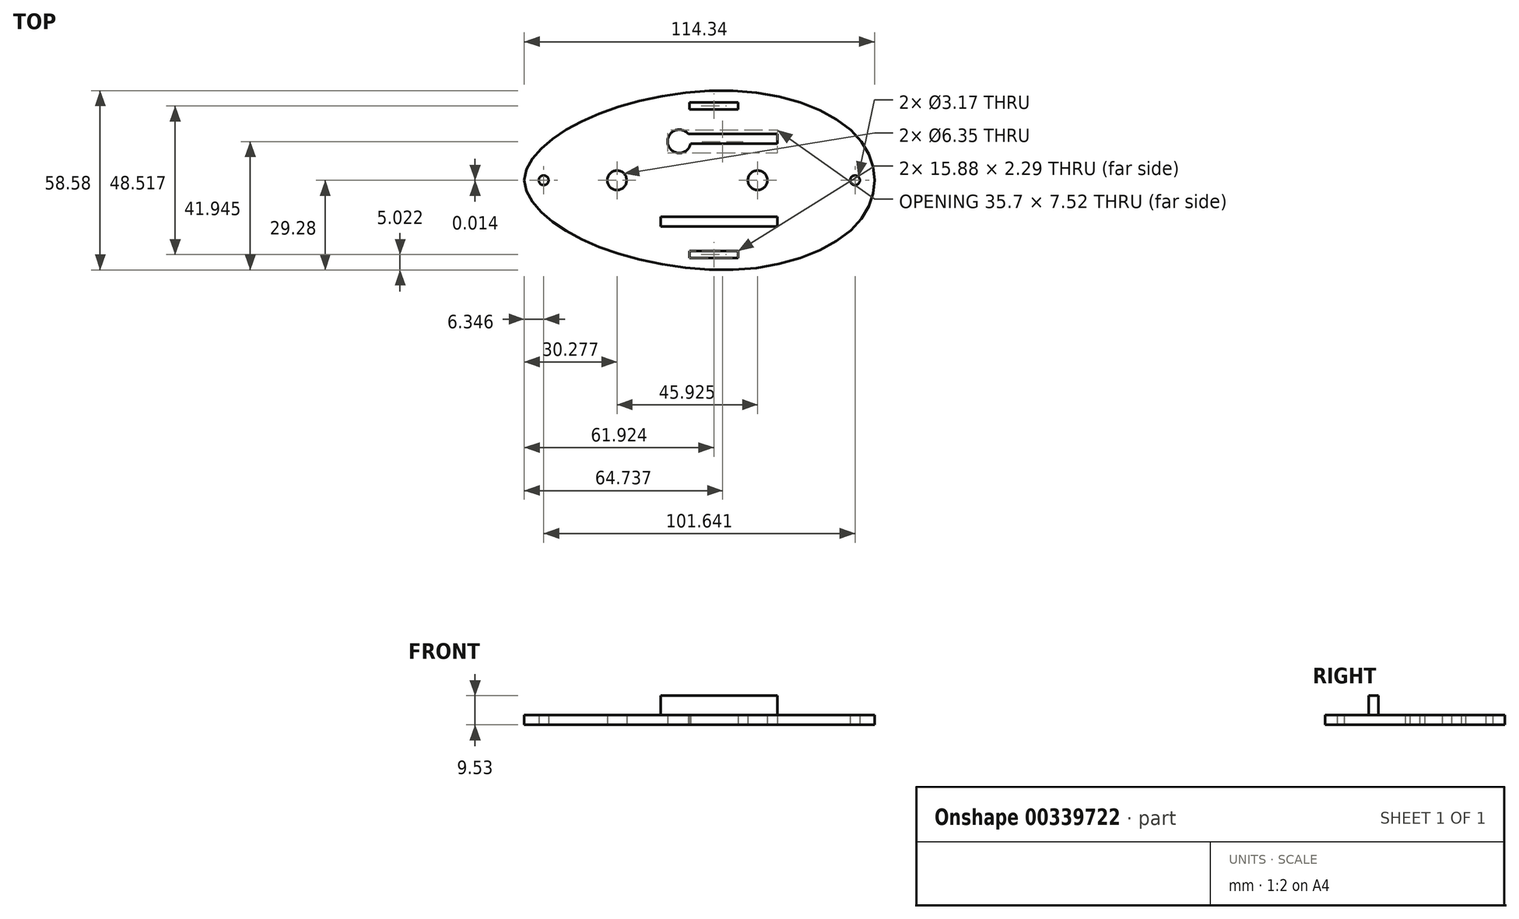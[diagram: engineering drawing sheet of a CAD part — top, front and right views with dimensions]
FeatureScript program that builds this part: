
annotation { "Feature Type Name" : "Feature", "Feature Type Description" : "" }
export const myFeature = defineFeature(function(context is Context, id is Id, definition is map)
    precondition{}
    {
        {
            var Q0;
            Q0=qCreatedBy(makeId("Top.planeOp"),FACE);
            var sketch = newSketch(context, id + "F0", { "sketchPlane" : qUnion([Q0])});
            skCircle(sketch, "E0", {"center": v(-26.88, 0) * mm, "radius": 3.18 * mm});
            skCircle(sketch, "E1", {"center": v(-50.81, 0) * mm, "radius": 1.59 * mm});
            skCircle(sketch, "E2", {"center": v(19.04, 0.01) * mm, "radius": 3.18 * mm});
            skCircle(sketch, "E3", {"center": v(50.83, 0) * mm, "radius": 1.59 * mm});
            skLineSegment(sketch, "E4", {"start": v(50.83, 0) * mm, "end": v(57.18, 0) * mm});
            skLineSegment(sketch, "E5", {"start": v(-50.81, 0) * mm, "end": v(-57.16, 0) * mm});
            skFitSpline(sketch, "E6", {"points": [v(-57.16, 0) * mm, v(-50.81, 11.11) * mm, v(-26.88, 23.81) * mm, v(19.04, 28.59) * mm, v(50.83, 15.08) * mm, v(57.18, 0) * mm, v(50.83, -15.08) * mm, v(19.04, -28.56) * mm, v(-26.88, -23.81) * mm, v(-50.81, -11.11) * mm, v(-57.16, 0) * mm]});
            skLineSegment(sketch, "E7", {"start": v(-3.17, 25.4) * mm, "end": v(12.7, 25.4) * mm});
            skLineSegment(sketch, "E8", {"start": v(-3.17, -25.4) * mm, "end": v(12.7, -25.4) * mm});
            skLineSegment(sketch, "E9", {"start": v(12.7, -25.4) * mm, "end": v(12.7, -23.12) * mm});
            skLineSegment(sketch, "E10", {"start": v(12.7, -23.12) * mm, "end": v(-3.17, -23.12) * mm});
            skLineSegment(sketch, "E11.trimOffspring", {"start": v(-3.17, -23.12) * mm, "end": v(-3.17, -25.4) * mm});
            skLineSegment(sketch, "E12.trimOffspring", {"start": v(12.7, 23.12) * mm, "end": v(12.7, 25.4) * mm});
            skLineSegment(sketch, "E13.trimOffspring", {"start": v(-3.17, 25.4) * mm, "end": v(-3.17, 23.12) * mm});
            skLineSegment(sketch, "E14.trimOffspring", {"start": v(12.7, 23.12) * mm, "end": v(-3.17, 23.12) * mm});
            skCircle(sketch, "E15", {"center": v(-6.56, 12.71) * mm, "radius": 3.81 * mm});
            skLineSegment(sketch, "E16", {"start": v(25.43, 15.08) * mm, "end": v(-3.58, 15.08) * mm});
            skLineSegment(sketch, "E17", {"start": v(57.18, 0) * mm, "end": v(-72.8, 0) * mm});
            skLineSegment(sketch, "E18.trimOffspring", {"start": v(25.43, -15.08) * mm, "end": v(-12.67, -15.08) * mm});
            skLineSegment(sketch, "E19.trimOffspring", {"start": v(25.43, 15.08) * mm, "end": v(25.43, 11.9) * mm});
            skLineSegment(sketch, "E20", {"start": v(25.43, 11.9) * mm, "end": v(-2.84, 11.9) * mm});
            skLineSegment(sketch, "E21", {"start": v(-12.67, -15.08) * mm, "end": v(-12.67, -11.9) * mm});
            skLineSegment(sketch, "E22", {"start": v(-12.67, -11.9) * mm, "end": v(25.43, -11.9) * mm});
            skLineSegment(sketch, "E23.trimOffspring", {"start": v(-3.58, 15.08) * mm, "end": v(25.43, 15.08) * mm});
            skLineSegment(sketch, "E24.trimOffspring", {"start": v(25.43, -11.9) * mm, "end": v(25.43, -15.08) * mm});
            skSolve(sketch);
        }
        {
            var Q0;
            Q0 = qSketchRegion(id + "F0", true);
            extrude(context, id + "F1", {"entities" : qUnion([Q0]), "depth" : 3.17 * mm});
        }
        {
            var Q0;
            Q0=makeQuery(id+"F0.imprint","IMPRINT",FACE,{"disambiguationData":[TD([[makeQuery(id+"F0.imprint","IMPRINT",EDGE,{"derivedFrom":sQuery(id+"F0.wireOp",EDGE,"E19.trimOffspring")}),-1.0]])]});
            var Q1;
            Q1=makeQuery(id+"F0.imprint","IMPRINT",FACE,{"disambiguationData":[TD([[makeQuery(id+"F0.imprint","IMPRINT",EDGE,{"derivedFrom":sQuery(id+"F0.wireOp",EDGE,"E18.trimOffspring")}),-1.0]])]});
            extrude(context, id + "F2", {"entities" : qUnion([Q0, Q1]), "operationType" : NewBodyOperationType.ADD, "depth" : 9.52 * mm});
        }
    });
